# Revit family: DCS_Revit_18_PBE1-24-N_or_L_Grill_90000776A
name_source: partatom
category: Specialty Equipment
revit_build: Autodesk Revit 2018 (Build: 20170223_1515(x64)
units: mm (PartAtom-declared; Revit-internal decimal feet)

## family parameters
Always vertical = Yes
Cut with Voids When Loaded = Yes
OmniClass Number = 23.40.40.14.17.27
OmniClass Title = Barbecues
Part Type = Normal
Room Calculation Point = No
Round Connector Dimension = Use Diameter
Shared = No
Work Plane-Based = No

## types (4) — shared parameters
Clearance - Below Combustible = 457 mm  [stored 1.49934 ft]
Clearance - Rear Combustible = 457 mm  [stored 1.49934 ft]
Clearance - Rear Non-Combustible = 76 mm  [stored 0.249344 ft]
Clearance - Side Combustible = 457 mm  [stored 1.49934 ft]
Clearance - Side Non-Combustible = 76 mm  [stored 0.249344 ft]
Connector Description - Electrical = 120 V, 15 A, GFI electrical outlet
Connector Description - Gas = Operating Pressure NG 4” WC, LPG 11” WC, Connection is 1/2” NPT female
Manufacturer = Fisher & Paykel
Material - Body = DCS - Stainless Steel
Model = PBE1-24-N or PBE1-24-L with BGB24IJS
URL = www.dcsappliances.com
Visibility - Clearance Required = Yes

## per-type parameters (varying)
| type | Cavity - Depth | Cavity - Height | Cavity - Width | Description | Product - Depth | Product - Height | Product - Width | Visibility - Clearance Required (Below Countertop) | Visibility - Cover | Visibility - Insulation Jacket |
| Power Burner | 578 mm  [stored 1.89633 ft] | 257 mm  [stored 0.843176 ft] | 572 mm | 24" Power Burner with 24" Insulation Jacket | 692 mm  [stored 2.27034 ft] | 312 mm  [stored 1.02362 ft] | 610 mm  [stored 2.00131 ft] | Yes | Yes | No |
| Power Burner with Insulated Jacket | 603 mm | 282 mm | 733 mm  [stored 2.40486 ft] | 24" Power Burner with 24" Insulated Jacket | 699 mm  [stored 2.29331 ft] | 342 mm  [stored 1.12205 ft] | 727 mm  [stored 2.38517 ft] | No | Yes | Yes |
| Power Burner with Insulated Jacket (without covers) | 603 mm | 282 mm | 733 mm  [stored 2.40486 ft] | 24" Power Burner with 24" Insulated Jacket | 699 mm  [stored 2.29331 ft] | 342 mm  [stored 1.12205 ft] | 727 mm  [stored 2.38517 ft] | No | No | Yes |
| Power Burner (without covers) | 578 mm  [stored 1.89633 ft] | 257 mm  [stored 0.843176 ft] | 572 mm | 24" Power Burner with 24" Insulated Jacket | 692 mm  [stored 2.27034 ft] | 312 mm  [stored 1.02362 ft] | 610 mm  [stored 2.00131 ft] | Yes | No | No |

note: [stored X ft] marks values corroborated as IEEE doubles in the binary element streams (Revit-internal decimal feet)

## geometry (parser evidence)
native form markers: Sweep x21
no freeform markers — native parametric forms only
